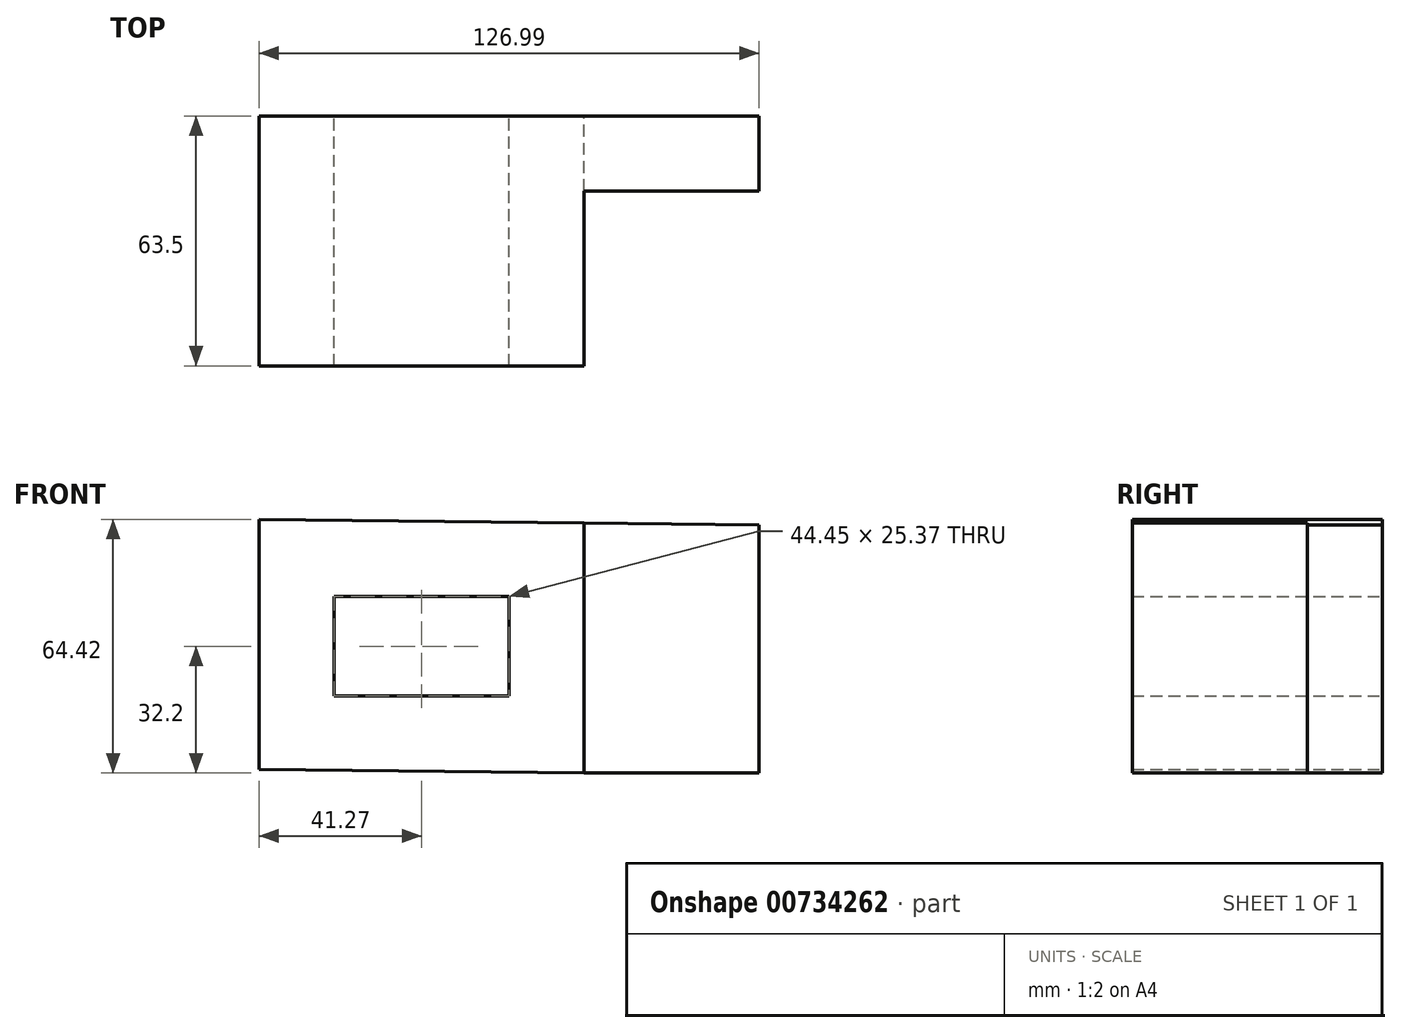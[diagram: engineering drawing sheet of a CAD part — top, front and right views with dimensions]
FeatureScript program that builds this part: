
annotation { "Feature Type Name" : "Feature", "Feature Type Description" : "" }
export const myFeature = defineFeature(function(context is Context, id is Id, definition is map)
    precondition{}
    {
        {
            var Q0;
            Q0=qCreatedBy(makeId("Front.planeOp"),FACE);
            var sketch = newSketch(context, id + "F0", { "sketchPlane" : qUnion([Q0])});
            skLineSegment(sketch, "E0.bottom", {"start": v(27.7, 16.9) * mm, "end": v(-16.75, 16.9) * mm});
            skLineSegment(sketch, "E0.top", {"start": v(27.7, -8.47) * mm, "end": v(-16.75, -8.47) * mm});
            skLineSegment(sketch, "E0.left", {"start": v(27.7, 16.9) * mm, "end": v(27.7, -8.47) * mm});
            skLineSegment(sketch, "E0.right", {"start": v(-16.75, 16.9) * mm, "end": v(-16.75, -8.47) * mm});
            skLineSegment(sketch, "E1", {"start": v(-35.8, 36.44) * mm, "end": v(-35.8, -27.06) * mm});
            skLineSegment(sketch, "E2", {"start": v(46.74, 35.52) * mm, "end": v(46.74, -27.98) * mm});
            skLineSegment(sketch, "E3", {"start": v(46.74, -27.98) * mm, "end": v(-35.8, -27.06) * mm});
            skLineSegment(sketch, "E4", {"start": v(-35.8, 36.44) * mm, "end": v(46.74, 35.52) * mm});
            skLineSegment(sketch, "E5", {"start": v(46.74, 35.52) * mm, "end": v(91.19, 35.03) * mm});
            skLineSegment(sketch, "E6", {"start": v(91.19, 35.03) * mm, "end": v(91.19, -27.98) * mm});
            skLineSegment(sketch, "E7", {"start": v(91.19, -27.98) * mm, "end": v(46.74, -27.98) * mm});
            skSolve(sketch);
        }
        {
            var Q0;
            Q0=makeQuery(id+"F0.imprint","IMPRINT",FACE,{"disambiguationData":[TD([[makeQuery(id+"F0.imprint","IMPRINT",EDGE,{"derivedFrom":sQuery(id+"F0.wireOp",EDGE,"E0.bottom")}),-1.0]])]});
            extrude(context, id + "F1", {"entities" : qUnion([Q0]), "depth" : 63.5 * mm, "offsetDistance" : 25.4 * mm});
        }
        {
            var Q0;
            Q0=makeQuery(id+"F0.imprint","IMPRINT",FACE,{"disambiguationData":[TD([[makeQuery(id+"F0.imprint","IMPRINT",EDGE,{"derivedFrom":sQuery(id+"F0.wireOp",EDGE,"E2")}),1.0]])]});
            extrude(context, id + "F2", {"entities" : qUnion([Q0]), "operationType" : NewBodyOperationType.ADD, "depth" : 19.05 * mm, "offsetDistance" : 25.4 * mm});
        }
    });
